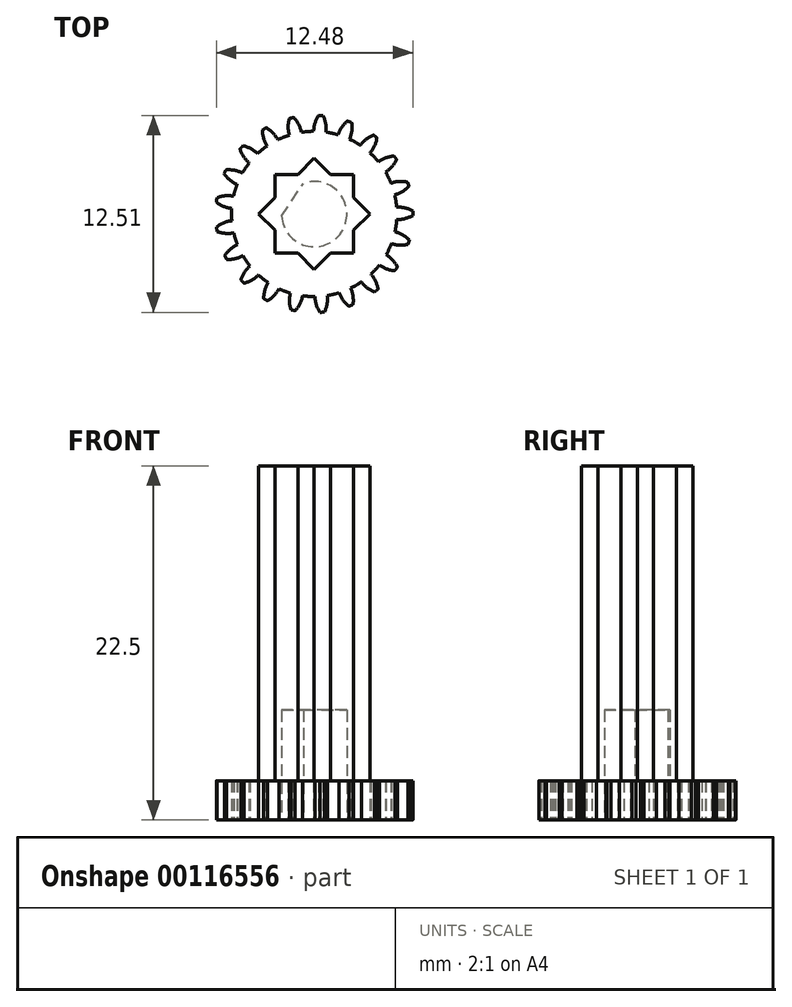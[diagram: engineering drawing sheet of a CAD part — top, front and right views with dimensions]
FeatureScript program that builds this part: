
annotation { "Feature Type Name" : "Feature", "Feature Type Description" : "" }
export const myFeature = defineFeature(function(context is Context, id is Id, definition is map)
    precondition{}
    {
        {
            var Q0;
            Q0=qCreatedBy(makeId("Top.planeOp"),FACE);
            var sketch = newSketch(context, id + "F0", { "sketchPlane" : qUnion([Q0])});
            skLineSegment(sketch, "E0", {"start": v(61.42, 3.14) * mm, "end": v(65.52, 3.14) * mm, "construction": true});
            skLineSegment(sketch, "E1", {"start": v(61.42, 3.14) * mm, "end": v(65.31, 4.4) * mm, "construction": true});
            skLineSegment(sketch, "E2", {"start": v(61.42, 3.14) * mm, "end": v(65.72, 3.82) * mm, "construction": true});
            skPoint(sketch, "E3.third.point", {"position": v(57.79, 0) * mm});
            skArc(sketch, "E4.MirrorCS", {"start": v(62.86, 3.22) * mm, "mid": v(63.38, 3.1) * mm, "end": v(63.92, 3.14) * mm});
            skArc(sketch, "E5.MirrorCS", {"start": v(62.86, 3.22) * mm, "mid": v(62.85, 3.3) * mm, "end": v(62.84, 3.36) * mm});
            skArc(sketch, "E6.MirrorCS", {"start": v(62.82, 3.5) * mm, "mid": v(62.83, 3.43) * mm, "end": v(62.84, 3.36) * mm});
            skArc(sketch, "E7.MirrorCS", {"start": v(62.82, 3.5) * mm, "mid": v(63.28, 3.78) * mm, "end": v(63.8, 3.9) * mm});
            skLineSegment(sketch, "E8", {"start": v(69.03, 4.34) * mm, "end": v(63.8, 3.9) * mm, "construction": true});
            skArc(sketch, "E9.1.0", {"start": v(63.34, 1.7) * mm, "mid": v(63.7, 2.1) * mm, "end": v(64.15, 2.39) * mm});
            skArc(sketch, "E9.1.1", {"start": v(63.34, 1.7) * mm, "mid": v(63.37, 1.64) * mm, "end": v(63.4, 1.58) * mm});
            skArc(sketch, "E9.1.2", {"start": v(63.46, 1.46) * mm, "mid": v(63.43, 1.52) * mm, "end": v(63.4, 1.58) * mm});
            skArc(sketch, "E9.1.3", {"start": v(63.46, 1.46) * mm, "mid": v(64, 1.5) * mm, "end": v(64.5, 1.68) * mm});
            skArc(sketch, "E9.2.0", {"start": v(64.37, 0.15) * mm, "mid": v(64.6, 0.63) * mm, "end": v(64.95, 1.04) * mm});
            skArc(sketch, "E9.2.1", {"start": v(64.37, 0.15) * mm, "mid": v(64.42, 0.1) * mm, "end": v(64.46, 0.05) * mm});
            skArc(sketch, "E9.2.2", {"start": v(64.56, -0.05) * mm, "mid": v(64.51, 0) * mm, "end": v(64.46, 0.05) * mm});
            skArc(sketch, "E9.2.3", {"start": v(64.56, -0.05) * mm, "mid": v(65.06, 0.14) * mm, "end": v(65.48, 0.47) * mm});
            skArc(sketch, "E9.3.0", {"start": v(65.81, -1.04) * mm, "mid": v(65.88, -0.5) * mm, "end": v(66.1, -0.02) * mm});
            skArc(sketch, "E9.3.1", {"start": v(65.81, -1.04) * mm, "mid": v(65.87, -1.07) * mm, "end": v(65.93, -1.1) * mm});
            skArc(sketch, "E9.3.2", {"start": v(66.06, -1.17) * mm, "mid": v(66, -1.14) * mm, "end": v(65.93, -1.1) * mm});
            skArc(sketch, "E9.3.3", {"start": v(66.06, -1.17) * mm, "mid": v(66.47, -0.84) * mm, "end": v(66.78, -0.4) * mm});
            skArc(sketch, "E9.4.0", {"start": v(67.54, -1.74) * mm, "mid": v(67.45, -1.22) * mm, "end": v(67.52, -0.69) * mm});
            skArc(sketch, "E9.4.1", {"start": v(67.54, -1.74) * mm, "mid": v(67.6, -1.76) * mm, "end": v(67.68, -1.78) * mm});
            skArc(sketch, "E9.4.2", {"start": v(67.81, -1.8) * mm, "mid": v(67.75, -1.8) * mm, "end": v(67.68, -1.78) * mm});
            skArc(sketch, "E9.4.3", {"start": v(67.81, -1.8) * mm, "mid": v(68.12, -1.36) * mm, "end": v(68.28, -0.85) * mm});
            skArc(sketch, "E9.5.0", {"start": v(69.4, -1.91) * mm, "mid": v(69.16, -1.43) * mm, "end": v(69.07, -0.9) * mm});
            skArc(sketch, "E9.5.1", {"start": v(69.4, -1.91) * mm, "mid": v(69.47, -1.9) * mm, "end": v(69.54, -1.9) * mm});
            skArc(sketch, "E9.5.2", {"start": v(69.68, -1.89) * mm, "mid": v(69.61, -1.9) * mm, "end": v(69.54, -1.9) * mm});
            skArc(sketch, "E9.5.3", {"start": v(69.68, -1.89) * mm, "mid": v(69.84, -1.38) * mm, "end": v(69.85, -0.84) * mm});
            skArc(sketch, "E9.6.0", {"start": v(71.23, -1.52) * mm, "mid": v(70.86, -1.14) * mm, "end": v(70.61, -0.66) * mm});
            skArc(sketch, "E9.6.1", {"start": v(71.23, -1.52) * mm, "mid": v(71.3, -1.5) * mm, "end": v(71.36, -1.47) * mm});
            skArc(sketch, "E9.6.2", {"start": v(71.49, -1.42) * mm, "mid": v(71.42, -1.45) * mm, "end": v(71.36, -1.47) * mm});
            skArc(sketch, "E9.6.3", {"start": v(71.49, -1.42) * mm, "mid": v(71.49, -0.88) * mm, "end": v(71.34, -0.37) * mm});
            skArc(sketch, "E9.7.0", {"start": v(72.86, -0.61) * mm, "mid": v(72.4, -0.35) * mm, "end": v(72.02, 0.03) * mm});
            skArc(sketch, "E9.7.1", {"start": v(72.86, -0.61) * mm, "mid": v(72.91, -0.57) * mm, "end": v(72.97, -0.53) * mm});
            skArc(sketch, "E9.7.2", {"start": v(73.08, -0.44) * mm, "mid": v(73.02, -0.48) * mm, "end": v(72.97, -0.53) * mm});
            skArc(sketch, "E9.7.3", {"start": v(73.08, -0.44) * mm, "mid": v(72.92, 0.07) * mm, "end": v(72.62, 0.52) * mm});
            skArc(sketch, "E9.8.0", {"start": v(74.15, 0.74) * mm, "mid": v(73.63, 0.85) * mm, "end": v(73.16, 1.1) * mm});
            skArc(sketch, "E9.8.1", {"start": v(74.15, 0.74) * mm, "mid": v(74.19, 0.8) * mm, "end": v(74.23, 0.85) * mm});
            skArc(sketch, "E9.8.2", {"start": v(74.3, 0.97) * mm, "mid": v(74.27, 0.9) * mm, "end": v(74.23, 0.85) * mm});
            skArc(sketch, "E9.8.3", {"start": v(74.3, 0.97) * mm, "mid": v(74, 1.41) * mm, "end": v(73.6, 1.75) * mm});
            skArc(sketch, "E9.9.0", {"start": v(74.98, 2.4) * mm, "mid": v(74.45, 2.36) * mm, "end": v(73.93, 2.46) * mm});
            skArc(sketch, "E9.9.1", {"start": v(74.98, 2.4) * mm, "mid": v(75, 2.47) * mm, "end": v(75.03, 2.54) * mm});
            skArc(sketch, "E9.9.2", {"start": v(75.06, 2.67) * mm, "mid": v(75.05, 2.6) * mm, "end": v(75.03, 2.54) * mm});
            skArc(sketch, "E9.9.3", {"start": v(75.06, 2.67) * mm, "mid": v(74.65, 3) * mm, "end": v(74.15, 3.21) * mm});
            skArc(sketch, "E9.10.0", {"start": v(75.29, 4.25) * mm, "mid": v(74.8, 4.05) * mm, "end": v(74.26, 4) * mm});
            skArc(sketch, "E9.10.1", {"start": v(75.29, 4.25) * mm, "mid": v(75.3, 4.32) * mm, "end": v(75.3, 4.39) * mm});
            skArc(sketch, "E9.10.2", {"start": v(75.29, 4.53) * mm, "mid": v(75.3, 4.46) * mm, "end": v(75.3, 4.39) * mm});
            skArc(sketch, "E9.10.3", {"start": v(75.29, 4.53) * mm, "mid": v(74.8, 4.72) * mm, "end": v(74.26, 4.77) * mm});
            skArc(sketch, "E9.11.0", {"start": v(75.04, 6.1) * mm, "mid": v(74.63, 5.76) * mm, "end": v(74.13, 5.55) * mm});
            skArc(sketch, "E9.11.1", {"start": v(75.04, 6.1) * mm, "mid": v(75.02, 6.17) * mm, "end": v(75, 6.23) * mm});
            skArc(sketch, "E9.11.2", {"start": v(74.95, 6.37) * mm, "mid": v(74.98, 6.3) * mm, "end": v(75, 6.23) * mm});
            skArc(sketch, "E9.11.3", {"start": v(74.95, 6.37) * mm, "mid": v(74.42, 6.4) * mm, "end": v(73.9, 6.3) * mm});
            skArc(sketch, "E9.12.0", {"start": v(74.25, 7.8) * mm, "mid": v(73.96, 7.35) * mm, "end": v(73.55, 7) * mm});
            skArc(sketch, "E9.12.1", {"start": v(74.25, 7.8) * mm, "mid": v(74.22, 7.85) * mm, "end": v(74.18, 7.91) * mm});
            skArc(sketch, "E9.12.2", {"start": v(74.1, 8.02) * mm, "mid": v(74.14, 7.97) * mm, "end": v(74.18, 7.91) * mm});
            skArc(sketch, "E9.12.3", {"start": v(74.1, 8.02) * mm, "mid": v(73.57, 7.9) * mm, "end": v(73.1, 7.65) * mm});
            skArc(sketch, "E9.13.0", {"start": v(73, 9.18) * mm, "mid": v(72.85, 8.67) * mm, "end": v(72.57, 8.22) * mm});
            skArc(sketch, "E9.13.1", {"start": v(73, 9.18) * mm, "mid": v(72.95, 9.23) * mm, "end": v(72.9, 9.27) * mm});
            skArc(sketch, "E9.13.2", {"start": v(72.78, 9.35) * mm, "mid": v(72.84, 9.31) * mm, "end": v(72.9, 9.27) * mm});
            skArc(sketch, "E9.13.3", {"start": v(72.78, 9.35) * mm, "mid": v(72.32, 9.09) * mm, "end": v(71.95, 8.7) * mm});
            skArc(sketch, "E9.14.0", {"start": v(71.4, 10.14) * mm, "mid": v(71.4, 9.6) * mm, "end": v(71.27, 9.09) * mm});
            skArc(sketch, "E9.14.1", {"start": v(71.4, 10.14) * mm, "mid": v(71.34, 10.17) * mm, "end": v(71.27, 10.2) * mm});
            skArc(sketch, "E9.14.2", {"start": v(71.14, 10.24) * mm, "mid": v(71.2, 10.22) * mm, "end": v(71.27, 10.2) * mm});
            skArc(sketch, "E9.14.3", {"start": v(71.14, 10.24) * mm, "mid": v(70.78, 9.85) * mm, "end": v(70.54, 9.37) * mm});
            skArc(sketch, "E9.15.0", {"start": v(69.59, 10.58) * mm, "mid": v(69.75, 10.07) * mm, "end": v(69.77, 9.54) * mm});
            skArc(sketch, "E9.15.1", {"start": v(69.59, 10.58) * mm, "mid": v(69.52, 10.59) * mm, "end": v(69.45, 10.6) * mm});
            skArc(sketch, "E9.15.2", {"start": v(69.3, 10.6) * mm, "mid": v(69.38, 10.6) * mm, "end": v(69.45, 10.6) * mm});
            skArc(sketch, "E9.15.3", {"start": v(69.3, 10.6) * mm, "mid": v(69.07, 10.12) * mm, "end": v(68.99, 9.6) * mm});
            skArc(sketch, "E9.16.0", {"start": v(67.72, 10.47) * mm, "mid": v(68.03, 10.03) * mm, "end": v(68.2, 9.53) * mm});
            skArc(sketch, "E9.16.1", {"start": v(67.72, 10.47) * mm, "mid": v(67.65, 10.46) * mm, "end": v(67.59, 10.44) * mm});
            skArc(sketch, "E9.16.2", {"start": v(67.45, 10.4) * mm, "mid": v(67.52, 10.42) * mm, "end": v(67.59, 10.44) * mm});
            skArc(sketch, "E9.16.3", {"start": v(67.45, 10.4) * mm, "mid": v(67.37, 9.88) * mm, "end": v(67.44, 9.35) * mm});
            skArc(sketch, "E9.17.0", {"start": v(65.97, 9.81) * mm, "mid": v(66.4, 9.49) * mm, "end": v(66.71, 9.05) * mm});
            skArc(sketch, "E9.17.1", {"start": v(65.97, 9.81) * mm, "mid": v(65.91, 9.78) * mm, "end": v(65.85, 9.75) * mm});
            skArc(sketch, "E9.17.2", {"start": v(65.73, 9.67) * mm, "mid": v(65.8, 9.7) * mm, "end": v(65.85, 9.75) * mm});
            skArc(sketch, "E9.17.3", {"start": v(65.73, 9.67) * mm, "mid": v(65.81, 9.14) * mm, "end": v(66.04, 8.66) * mm});
            skArc(sketch, "E9.18.0", {"start": v(64.5, 8.67) * mm, "mid": v(65, 8.48) * mm, "end": v(65.43, 8.16) * mm});
            skArc(sketch, "E9.18.1", {"start": v(64.5, 8.67) * mm, "mid": v(64.45, 8.62) * mm, "end": v(64.4, 8.57) * mm});
            skArc(sketch, "E9.18.2", {"start": v(64.3, 8.47) * mm, "mid": v(64.35, 8.52) * mm, "end": v(64.4, 8.57) * mm});
            skArc(sketch, "E9.18.3", {"start": v(64.3, 8.47) * mm, "mid": v(64.54, 7.98) * mm, "end": v(64.9, 7.59) * mm});
            skArc(sketch, "E9.19.0", {"start": v(63.42, 7.14) * mm, "mid": v(63.96, 7.11) * mm, "end": v(64.46, 6.93) * mm});
            skArc(sketch, "E9.19.1", {"start": v(63.42, 7.14) * mm, "mid": v(63.4, 7.08) * mm, "end": v(63.36, 7.02) * mm});
            skArc(sketch, "E9.19.2", {"start": v(63.3, 6.9) * mm, "mid": v(63.33, 6.96) * mm, "end": v(63.36, 7.02) * mm});
            skArc(sketch, "E9.19.3", {"start": v(63.3, 6.9) * mm, "mid": v(63.67, 6.5) * mm, "end": v(64.12, 6.22) * mm});
            skArc(sketch, "E9.20.0", {"start": v(62.85, 5.37) * mm, "mid": v(63.36, 5.5) * mm, "end": v(63.9, 5.47) * mm});
            skArc(sketch, "E9.20.1", {"start": v(62.85, 5.37) * mm, "mid": v(62.83, 5.3) * mm, "end": v(62.82, 5.23) * mm});
            skArc(sketch, "E9.20.2", {"start": v(62.8, 5.1) * mm, "mid": v(62.81, 5.16) * mm, "end": v(62.82, 5.23) * mm});
            skArc(sketch, "E9.20.3", {"start": v(62.8, 5.1) * mm, "mid": v(63.27, 4.82) * mm, "end": v(63.79, 4.7) * mm});
            skPoint(sketch, "E9.center", {"position": v(69.03, 4.34) * mm});
            skCircle(sketch, "E10", {"center": v(69.03, 4.34) * mm, "radius": 5.25 * mm});
            skSolve(sketch);
        }
        {
            var Q0;
            Q0=qSketchRegion(id+"F0",true);
            extrude(context, id + "F1", {"entities" : qUnion([Q0]), "depth" : 2.5 * mm});
        }
        {
            var Q0;
            Q0=makeQuery(id+"F1.opExtrude","CAP_FACE",FACE,{"disambiguationData":[OSD([sQuery(id+"F0.wireOp",EDGE,"E4.MirrorCS"),sQuery(id+"F0.wireOp",EDGE,"E5.MirrorCS"),sQuery(id+"F0.wireOp",EDGE,"E6.MirrorCS"),sQuery(id+"F0.wireOp",EDGE,"E7.MirrorCS"),sQuery(id+"F0.wireOp",EDGE,"3aad1c11-f46f-48f3-83f1-c81cc0587eb40.MirrorCS"),sQuery(id+"F0.wireOp",EDGE,"261d038e-785b-489d-9701-d77bc27e36f7.1.0"),sQuery(id+"F0.wireOp",EDGE,"261d038e-785b-489d-9701-d77bc27e36f7.1.1"),sQuery(id+"F0.wireOp",EDGE,"261d038e-785b-489d-9701-d77bc27e36f7.1.2"),sQuery(id+"F0.wireOp",EDGE,"261d038e-785b-489d-9701-d77bc27e36f7.1.3"),sQuery(id+"F0.wireOp",EDGE,"261d038e-785b-489d-9701-d77bc27e36f7.1.4"),sQuery(id+"F0.wireOp",EDGE,"261d038e-785b-489d-9701-d77bc27e36f7.2.0"),sQuery(id+"F0.wireOp",EDGE,"261d038e-785b-489d-9701-d77bc27e36f7.2.1"),sQuery(id+"F0.wireOp",EDGE,"261d038e-785b-489d-9701-d77bc27e36f7.2.2"),sQuery(id+"F0.wireOp",EDGE,"261d038e-785b-489d-9701-d77bc27e36f7.2.3"),sQuery(id+"F0.wireOp",EDGE,"261d038e-785b-489d-9701-d77bc27e36f7.2.4"),sQuery(id+"F0.wireOp",EDGE,"261d038e-785b-489d-9701-d77bc27e36f7.3.0"),sQuery(id+"F0.wireOp",EDGE,"261d038e-785b-489d-9701-d77bc27e36f7.3.1"),sQuery(id+"F0.wireOp",EDGE,"261d038e-785b-489d-9701-d77bc27e36f7.3.2"),sQuery(id+"F0.wireOp",EDGE,"261d038e-785b-489d-9701-d77bc27e36f7.3.3"),sQuery(id+"F0.wireOp",EDGE,"261d038e-785b-489d-9701-d77bc27e36f7.3.4"),sQuery(id+"F0.wireOp",EDGE,"261d038e-785b-489d-9701-d77bc27e36f7.4.0"),sQuery(id+"F0.wireOp",EDGE,"261d038e-785b-489d-9701-d77bc27e36f7.4.1"),sQuery(id+"F0.wireOp",EDGE,"261d038e-785b-489d-9701-d77bc27e36f7.4.2"),sQuery(id+"F0.wireOp",EDGE,"261d038e-785b-489d-9701-d77bc27e36f7.4.3"),sQuery(id+"F0.wireOp",EDGE,"261d038e-785b-489d-9701-d77bc27e36f7.4.4"),sQuery(id+"F0.wireOp",EDGE,"261d038e-785b-489d-9701-d77bc27e36f7.5.0"),sQuery(id+"F0.wireOp",EDGE,"261d038e-785b-489d-9701-d77bc27e36f7.5.1"),sQuery(id+"F0.wireOp",EDGE,"261d038e-785b-489d-9701-d77bc27e36f7.5.2"),sQuery(id+"F0.wireOp",EDGE,"261d038e-785b-489d-9701-d77bc27e36f7.5.3"),sQuery(id+"F0.wireOp",EDGE,"261d038e-785b-489d-9701-d77bc27e36f7.5.4"),sQuery(id+"F0.wireOp",EDGE,"261d038e-785b-489d-9701-d77bc27e36f7.6.0"),sQuery(id+"F0.wireOp",EDGE,"261d038e-785b-489d-9701-d77bc27e36f7.6.1"),sQuery(id+"F0.wireOp",EDGE,"261d038e-785b-489d-9701-d77bc27e36f7.6.2"),sQuery(id+"F0.wireOp",EDGE,"261d038e-785b-489d-9701-d77bc27e36f7.6.3"),sQuery(id+"F0.wireOp",EDGE,"261d038e-785b-489d-9701-d77bc27e36f7.6.4"),sQuery(id+"F0.wireOp",EDGE,"261d038e-785b-489d-9701-d77bc27e36f7.7.0"),sQuery(id+"F0.wireOp",EDGE,"261d038e-785b-489d-9701-d77bc27e36f7.7.1"),sQuery(id+"F0.wireOp",EDGE,"261d038e-785b-489d-9701-d77bc27e36f7.7.2"),sQuery(id+"F0.wireOp",EDGE,"261d038e-785b-489d-9701-d77bc27e36f7.7.3"),sQuery(id+"F0.wireOp",EDGE,"261d038e-785b-489d-9701-d77bc27e36f7.7.4"),sQuery(id+"F0.wireOp",EDGE,"261d038e-785b-489d-9701-d77bc27e36f7.8.0"),sQuery(id+"F0.wireOp",EDGE,"261d038e-785b-489d-9701-d77bc27e36f7.8.1"),sQuery(id+"F0.wireOp",EDGE,"261d038e-785b-489d-9701-d77bc27e36f7.8.2"),sQuery(id+"F0.wireOp",EDGE,"261d038e-785b-489d-9701-d77bc27e36f7.8.3"),sQuery(id+"F0.wireOp",EDGE,"261d038e-785b-489d-9701-d77bc27e36f7.8.4"),sQuery(id+"F0.wireOp",EDGE,"261d038e-785b-489d-9701-d77bc27e36f7.9.0"),sQuery(id+"F0.wireOp",EDGE,"261d038e-785b-489d-9701-d77bc27e36f7.9.1"),sQuery(id+"F0.wireOp",EDGE,"261d038e-785b-489d-9701-d77bc27e36f7.9.2"),sQuery(id+"F0.wireOp",EDGE,"261d038e-785b-489d-9701-d77bc27e36f7.9.3"),sQuery(id+"F0.wireOp",EDGE,"261d038e-785b-489d-9701-d77bc27e36f7.9.4"),sQuery(id+"F0.wireOp",EDGE,"261d038e-785b-489d-9701-d77bc27e36f7.10.0"),sQuery(id+"F0.wireOp",EDGE,"261d038e-785b-489d-9701-d77bc27e36f7.10.1"),sQuery(id+"F0.wireOp",EDGE,"261d038e-785b-489d-9701-d77bc27e36f7.10.2"),sQuery(id+"F0.wireOp",EDGE,"261d038e-785b-489d-9701-d77bc27e36f7.10.3"),sQuery(id+"F0.wireOp",EDGE,"261d038e-785b-489d-9701-d77bc27e36f7.10.4"),sQuery(id+"F0.wireOp",EDGE,"261d038e-785b-489d-9701-d77bc27e36f7.11.0"),sQuery(id+"F0.wireOp",EDGE,"261d038e-785b-489d-9701-d77bc27e36f7.11.1"),sQuery(id+"F0.wireOp",EDGE,"261d038e-785b-489d-9701-d77bc27e36f7.11.2"),sQuery(id+"F0.wireOp",EDGE,"261d038e-785b-489d-9701-d77bc27e36f7.11.3"),sQuery(id+"F0.wireOp",EDGE,"261d038e-785b-489d-9701-d77bc27e36f7.11.4"),sQuery(id+"F0.wireOp",EDGE,"261d038e-785b-489d-9701-d77bc27e36f7.12.0"),sQuery(id+"F0.wireOp",EDGE,"261d038e-785b-489d-9701-d77bc27e36f7.12.1"),sQuery(id+"F0.wireOp",EDGE,"261d038e-785b-489d-9701-d77bc27e36f7.12.2"),sQuery(id+"F0.wireOp",EDGE,"261d038e-785b-489d-9701-d77bc27e36f7.12.3"),sQuery(id+"F0.wireOp",EDGE,"261d038e-785b-489d-9701-d77bc27e36f7.12.4"),sQuery(id+"F0.wireOp",EDGE,"261d038e-785b-489d-9701-d77bc27e36f7.13.0"),sQuery(id+"F0.wireOp",EDGE,"261d038e-785b-489d-9701-d77bc27e36f7.13.1"),sQuery(id+"F0.wireOp",EDGE,"261d038e-785b-489d-9701-d77bc27e36f7.13.2"),sQuery(id+"F0.wireOp",EDGE,"261d038e-785b-489d-9701-d77bc27e36f7.13.3"),sQuery(id+"F0.wireOp",EDGE,"261d038e-785b-489d-9701-d77bc27e36f7.13.4"),sQuery(id+"F0.wireOp",EDGE,"261d038e-785b-489d-9701-d77bc27e36f7.14.0"),sQuery(id+"F0.wireOp",EDGE,"261d038e-785b-489d-9701-d77bc27e36f7.14.1"),sQuery(id+"F0.wireOp",EDGE,"261d038e-785b-489d-9701-d77bc27e36f7.14.2"),sQuery(id+"F0.wireOp",EDGE,"261d038e-785b-489d-9701-d77bc27e36f7.14.3"),sQuery(id+"F0.wireOp",EDGE,"261d038e-785b-489d-9701-d77bc27e36f7.14.4"),sQuery(id+"F0.wireOp",EDGE,"261d038e-785b-489d-9701-d77bc27e36f7.15.0"),sQuery(id+"F0.wireOp",EDGE,"261d038e-785b-489d-9701-d77bc27e36f7.15.1"),sQuery(id+"F0.wireOp",EDGE,"261d038e-785b-489d-9701-d77bc27e36f7.15.2"),sQuery(id+"F0.wireOp",EDGE,"261d038e-785b-489d-9701-d77bc27e36f7.15.3"),sQuery(id+"F0.wireOp",EDGE,"261d038e-785b-489d-9701-d77bc27e36f7.15.4"),sQuery(id+"F0.wireOp",EDGE,"261d038e-785b-489d-9701-d77bc27e36f7.16.0"),sQuery(id+"F0.wireOp",EDGE,"261d038e-785b-489d-9701-d77bc27e36f7.16.1"),sQuery(id+"F0.wireOp",EDGE,"261d038e-785b-489d-9701-d77bc27e36f7.16.2"),sQuery(id+"F0.wireOp",EDGE,"261d038e-785b-489d-9701-d77bc27e36f7.16.3"),sQuery(id+"F0.wireOp",EDGE,"261d038e-785b-489d-9701-d77bc27e36f7.16.4"),sQuery(id+"F0.wireOp",EDGE,"261d038e-785b-489d-9701-d77bc27e36f7.17.0"),sQuery(id+"F0.wireOp",EDGE,"261d038e-785b-489d-9701-d77bc27e36f7.17.1"),sQuery(id+"F0.wireOp",EDGE,"261d038e-785b-489d-9701-d77bc27e36f7.17.2"),sQuery(id+"F0.wireOp",EDGE,"261d038e-785b-489d-9701-d77bc27e36f7.17.3"),sQuery(id+"F0.wireOp",EDGE,"261d038e-785b-489d-9701-d77bc27e36f7.17.4"),sQuery(id+"F0.wireOp",EDGE,"261d038e-785b-489d-9701-d77bc27e36f7.18.0"),sQuery(id+"F0.wireOp",EDGE,"261d038e-785b-489d-9701-d77bc27e36f7.18.1"),sQuery(id+"F0.wireOp",EDGE,"261d038e-785b-489d-9701-d77bc27e36f7.18.2"),sQuery(id+"F0.wireOp",EDGE,"261d038e-785b-489d-9701-d77bc27e36f7.18.3"),sQuery(id+"F0.wireOp",EDGE,"261d038e-785b-489d-9701-d77bc27e36f7.18.4"),sQuery(id+"F0.wireOp",EDGE,"261d038e-785b-489d-9701-d77bc27e36f7.19.0"),sQuery(id+"F0.wireOp",EDGE,"261d038e-785b-489d-9701-d77bc27e36f7.19.1"),sQuery(id+"F0.wireOp",EDGE,"261d038e-785b-489d-9701-d77bc27e36f7.19.2"),sQuery(id+"F0.wireOp",EDGE,"261d038e-785b-489d-9701-d77bc27e36f7.19.3"),sQuery(id+"F0.wireOp",EDGE,"261d038e-785b-489d-9701-d77bc27e36f7.19.4"),sQuery(id+"F0.wireOp",EDGE,"f45ad2ee-8b84-45a9-bb91-348b52f7b137.4.20.0"),sQuery(id+"F0.wireOp",EDGE,"f45ad2ee-8b84-45a9-bb91-348b52f7b137.8.20.0"),sQuery(id+"F0.wireOp",EDGE,"f45ad2ee-8b84-45a9-bb91-348b52f7b137.12.20.0"),sQuery(id+"F0.wireOp",EDGE,"f45ad2ee-8b84-45a9-bb91-348b52f7b137.15.20.0"),sQuery(id+"F0.wireOp",EDGE,"f45ad2ee-8b84-45a9-bb91-348b52f7b137.16.20.0")])],"isStart":false});
            var sketch = newSketch(context, id + "F2", { "sketchPlane" : qUnion([Q0])});
            skLineSegment(sketch, "E11.bottom", {"start": v(71.53, 1.84) * mm, "end": v(66.53, 1.84) * mm});
            skLineSegment(sketch, "E11.top", {"start": v(71.53, 6.84) * mm, "end": v(66.53, 6.84) * mm});
            skLineSegment(sketch, "E11.left", {"start": v(71.53, 1.84) * mm, "end": v(71.53, 6.84) * mm});
            skLineSegment(sketch, "E11.right", {"start": v(66.53, 1.84) * mm, "end": v(66.53, 6.84) * mm});
            skPoint(sketch, "E11.middle", {"position": v(69.03, 4.34) * mm});
            skLineSegment(sketch, "E12", {"start": v(65.5, 4.34) * mm, "end": v(69.03, 7.88) * mm});
            skLineSegment(sketch, "E13", {"start": v(69.03, 7.88) * mm, "end": v(72.56, 4.34) * mm});
            skLineSegment(sketch, "E14", {"start": v(72.56, 4.34) * mm, "end": v(69.03, 0.8) * mm});
            skLineSegment(sketch, "E15", {"start": v(69.03, 0.8) * mm, "end": v(65.5, 4.34) * mm});
            skLineSegment(sketch, "E16", {"start": v(68.6, 9.57) * mm, "end": v(69.54, -1.9) * mm, "construction": true});
            skLineSegment(sketch, "E17", {"start": v(64, 5.85) * mm, "end": v(75.03, 2.54) * mm, "construction": true});
            skSolve(sketch);
        }
        {
            var Q0;
            Q0=qSketchRegion(id+"F2",true);
            extrude(context, id + "F3", {"entities" : qUnion([Q0]), "operationType" : NewBodyOperationType.ADD, "depth" : 20 * mm});
        }
        {
            var Q0;
            Q0=makeQuery(id+"F1.opExtrude","CAP_FACE",FACE,{"disambiguationData":[OSD([sQuery(id+"F0.wireOp",EDGE,"E4.MirrorCS"),sQuery(id+"F0.wireOp",EDGE,"E5.MirrorCS"),sQuery(id+"F0.wireOp",EDGE,"E6.MirrorCS"),sQuery(id+"F0.wireOp",EDGE,"E7.MirrorCS"),sQuery(id+"F0.wireOp",EDGE,"3aad1c11-f46f-48f3-83f1-c81cc0587eb40.MirrorCS"),sQuery(id+"F0.wireOp",EDGE,"261d038e-785b-489d-9701-d77bc27e36f7.1.0"),sQuery(id+"F0.wireOp",EDGE,"261d038e-785b-489d-9701-d77bc27e36f7.1.1"),sQuery(id+"F0.wireOp",EDGE,"261d038e-785b-489d-9701-d77bc27e36f7.1.2"),sQuery(id+"F0.wireOp",EDGE,"261d038e-785b-489d-9701-d77bc27e36f7.1.3"),sQuery(id+"F0.wireOp",EDGE,"261d038e-785b-489d-9701-d77bc27e36f7.1.4"),sQuery(id+"F0.wireOp",EDGE,"261d038e-785b-489d-9701-d77bc27e36f7.2.0"),sQuery(id+"F0.wireOp",EDGE,"261d038e-785b-489d-9701-d77bc27e36f7.2.1"),sQuery(id+"F0.wireOp",EDGE,"261d038e-785b-489d-9701-d77bc27e36f7.2.2"),sQuery(id+"F0.wireOp",EDGE,"261d038e-785b-489d-9701-d77bc27e36f7.2.3"),sQuery(id+"F0.wireOp",EDGE,"261d038e-785b-489d-9701-d77bc27e36f7.2.4"),sQuery(id+"F0.wireOp",EDGE,"261d038e-785b-489d-9701-d77bc27e36f7.3.0"),sQuery(id+"F0.wireOp",EDGE,"261d038e-785b-489d-9701-d77bc27e36f7.3.1"),sQuery(id+"F0.wireOp",EDGE,"261d038e-785b-489d-9701-d77bc27e36f7.3.2"),sQuery(id+"F0.wireOp",EDGE,"261d038e-785b-489d-9701-d77bc27e36f7.3.3"),sQuery(id+"F0.wireOp",EDGE,"261d038e-785b-489d-9701-d77bc27e36f7.3.4"),sQuery(id+"F0.wireOp",EDGE,"261d038e-785b-489d-9701-d77bc27e36f7.4.0"),sQuery(id+"F0.wireOp",EDGE,"261d038e-785b-489d-9701-d77bc27e36f7.4.1"),sQuery(id+"F0.wireOp",EDGE,"261d038e-785b-489d-9701-d77bc27e36f7.4.2"),sQuery(id+"F0.wireOp",EDGE,"261d038e-785b-489d-9701-d77bc27e36f7.4.3"),sQuery(id+"F0.wireOp",EDGE,"261d038e-785b-489d-9701-d77bc27e36f7.4.4"),sQuery(id+"F0.wireOp",EDGE,"261d038e-785b-489d-9701-d77bc27e36f7.5.0"),sQuery(id+"F0.wireOp",EDGE,"261d038e-785b-489d-9701-d77bc27e36f7.5.1"),sQuery(id+"F0.wireOp",EDGE,"261d038e-785b-489d-9701-d77bc27e36f7.5.2"),sQuery(id+"F0.wireOp",EDGE,"261d038e-785b-489d-9701-d77bc27e36f7.5.3"),sQuery(id+"F0.wireOp",EDGE,"261d038e-785b-489d-9701-d77bc27e36f7.5.4"),sQuery(id+"F0.wireOp",EDGE,"261d038e-785b-489d-9701-d77bc27e36f7.6.0"),sQuery(id+"F0.wireOp",EDGE,"261d038e-785b-489d-9701-d77bc27e36f7.6.1"),sQuery(id+"F0.wireOp",EDGE,"261d038e-785b-489d-9701-d77bc27e36f7.6.2"),sQuery(id+"F0.wireOp",EDGE,"261d038e-785b-489d-9701-d77bc27e36f7.6.3"),sQuery(id+"F0.wireOp",EDGE,"261d038e-785b-489d-9701-d77bc27e36f7.6.4"),sQuery(id+"F0.wireOp",EDGE,"261d038e-785b-489d-9701-d77bc27e36f7.7.0"),sQuery(id+"F0.wireOp",EDGE,"261d038e-785b-489d-9701-d77bc27e36f7.7.1"),sQuery(id+"F0.wireOp",EDGE,"261d038e-785b-489d-9701-d77bc27e36f7.7.2"),sQuery(id+"F0.wireOp",EDGE,"261d038e-785b-489d-9701-d77bc27e36f7.7.3"),sQuery(id+"F0.wireOp",EDGE,"261d038e-785b-489d-9701-d77bc27e36f7.7.4"),sQuery(id+"F0.wireOp",EDGE,"261d038e-785b-489d-9701-d77bc27e36f7.8.0"),sQuery(id+"F0.wireOp",EDGE,"261d038e-785b-489d-9701-d77bc27e36f7.8.1"),sQuery(id+"F0.wireOp",EDGE,"261d038e-785b-489d-9701-d77bc27e36f7.8.2"),sQuery(id+"F0.wireOp",EDGE,"261d038e-785b-489d-9701-d77bc27e36f7.8.3"),sQuery(id+"F0.wireOp",EDGE,"261d038e-785b-489d-9701-d77bc27e36f7.8.4"),sQuery(id+"F0.wireOp",EDGE,"261d038e-785b-489d-9701-d77bc27e36f7.9.0"),sQuery(id+"F0.wireOp",EDGE,"261d038e-785b-489d-9701-d77bc27e36f7.9.1"),sQuery(id+"F0.wireOp",EDGE,"261d038e-785b-489d-9701-d77bc27e36f7.9.2"),sQuery(id+"F0.wireOp",EDGE,"261d038e-785b-489d-9701-d77bc27e36f7.9.3"),sQuery(id+"F0.wireOp",EDGE,"261d038e-785b-489d-9701-d77bc27e36f7.9.4"),sQuery(id+"F0.wireOp",EDGE,"261d038e-785b-489d-9701-d77bc27e36f7.10.0"),sQuery(id+"F0.wireOp",EDGE,"261d038e-785b-489d-9701-d77bc27e36f7.10.1"),sQuery(id+"F0.wireOp",EDGE,"261d038e-785b-489d-9701-d77bc27e36f7.10.2"),sQuery(id+"F0.wireOp",EDGE,"261d038e-785b-489d-9701-d77bc27e36f7.10.3"),sQuery(id+"F0.wireOp",EDGE,"261d038e-785b-489d-9701-d77bc27e36f7.10.4"),sQuery(id+"F0.wireOp",EDGE,"261d038e-785b-489d-9701-d77bc27e36f7.11.0"),sQuery(id+"F0.wireOp",EDGE,"261d038e-785b-489d-9701-d77bc27e36f7.11.1"),sQuery(id+"F0.wireOp",EDGE,"261d038e-785b-489d-9701-d77bc27e36f7.11.2"),sQuery(id+"F0.wireOp",EDGE,"261d038e-785b-489d-9701-d77bc27e36f7.11.3"),sQuery(id+"F0.wireOp",EDGE,"261d038e-785b-489d-9701-d77bc27e36f7.11.4"),sQuery(id+"F0.wireOp",EDGE,"261d038e-785b-489d-9701-d77bc27e36f7.12.0"),sQuery(id+"F0.wireOp",EDGE,"261d038e-785b-489d-9701-d77bc27e36f7.12.1"),sQuery(id+"F0.wireOp",EDGE,"261d038e-785b-489d-9701-d77bc27e36f7.12.2"),sQuery(id+"F0.wireOp",EDGE,"261d038e-785b-489d-9701-d77bc27e36f7.12.3"),sQuery(id+"F0.wireOp",EDGE,"261d038e-785b-489d-9701-d77bc27e36f7.12.4"),sQuery(id+"F0.wireOp",EDGE,"261d038e-785b-489d-9701-d77bc27e36f7.13.0"),sQuery(id+"F0.wireOp",EDGE,"261d038e-785b-489d-9701-d77bc27e36f7.13.1"),sQuery(id+"F0.wireOp",EDGE,"261d038e-785b-489d-9701-d77bc27e36f7.13.2"),sQuery(id+"F0.wireOp",EDGE,"261d038e-785b-489d-9701-d77bc27e36f7.13.3"),sQuery(id+"F0.wireOp",EDGE,"261d038e-785b-489d-9701-d77bc27e36f7.13.4"),sQuery(id+"F0.wireOp",EDGE,"261d038e-785b-489d-9701-d77bc27e36f7.14.0"),sQuery(id+"F0.wireOp",EDGE,"261d038e-785b-489d-9701-d77bc27e36f7.14.1"),sQuery(id+"F0.wireOp",EDGE,"261d038e-785b-489d-9701-d77bc27e36f7.14.2"),sQuery(id+"F0.wireOp",EDGE,"261d038e-785b-489d-9701-d77bc27e36f7.14.3"),sQuery(id+"F0.wireOp",EDGE,"261d038e-785b-489d-9701-d77bc27e36f7.14.4"),sQuery(id+"F0.wireOp",EDGE,"261d038e-785b-489d-9701-d77bc27e36f7.15.0"),sQuery(id+"F0.wireOp",EDGE,"261d038e-785b-489d-9701-d77bc27e36f7.15.1"),sQuery(id+"F0.wireOp",EDGE,"261d038e-785b-489d-9701-d77bc27e36f7.15.2"),sQuery(id+"F0.wireOp",EDGE,"261d038e-785b-489d-9701-d77bc27e36f7.15.3"),sQuery(id+"F0.wireOp",EDGE,"261d038e-785b-489d-9701-d77bc27e36f7.15.4"),sQuery(id+"F0.wireOp",EDGE,"261d038e-785b-489d-9701-d77bc27e36f7.16.0"),sQuery(id+"F0.wireOp",EDGE,"261d038e-785b-489d-9701-d77bc27e36f7.16.1"),sQuery(id+"F0.wireOp",EDGE,"261d038e-785b-489d-9701-d77bc27e36f7.16.2"),sQuery(id+"F0.wireOp",EDGE,"261d038e-785b-489d-9701-d77bc27e36f7.16.3"),sQuery(id+"F0.wireOp",EDGE,"261d038e-785b-489d-9701-d77bc27e36f7.16.4"),sQuery(id+"F0.wireOp",EDGE,"261d038e-785b-489d-9701-d77bc27e36f7.17.0"),sQuery(id+"F0.wireOp",EDGE,"261d038e-785b-489d-9701-d77bc27e36f7.17.1"),sQuery(id+"F0.wireOp",EDGE,"261d038e-785b-489d-9701-d77bc27e36f7.17.2"),sQuery(id+"F0.wireOp",EDGE,"261d038e-785b-489d-9701-d77bc27e36f7.17.3"),sQuery(id+"F0.wireOp",EDGE,"261d038e-785b-489d-9701-d77bc27e36f7.17.4"),sQuery(id+"F0.wireOp",EDGE,"261d038e-785b-489d-9701-d77bc27e36f7.18.0"),sQuery(id+"F0.wireOp",EDGE,"261d038e-785b-489d-9701-d77bc27e36f7.18.1"),sQuery(id+"F0.wireOp",EDGE,"261d038e-785b-489d-9701-d77bc27e36f7.18.2"),sQuery(id+"F0.wireOp",EDGE,"261d038e-785b-489d-9701-d77bc27e36f7.18.3"),sQuery(id+"F0.wireOp",EDGE,"261d038e-785b-489d-9701-d77bc27e36f7.18.4"),sQuery(id+"F0.wireOp",EDGE,"261d038e-785b-489d-9701-d77bc27e36f7.19.0"),sQuery(id+"F0.wireOp",EDGE,"261d038e-785b-489d-9701-d77bc27e36f7.19.1"),sQuery(id+"F0.wireOp",EDGE,"261d038e-785b-489d-9701-d77bc27e36f7.19.2"),sQuery(id+"F0.wireOp",EDGE,"261d038e-785b-489d-9701-d77bc27e36f7.19.3"),sQuery(id+"F0.wireOp",EDGE,"261d038e-785b-489d-9701-d77bc27e36f7.19.4"),sQuery(id+"F0.wireOp",EDGE,"f45ad2ee-8b84-45a9-bb91-348b52f7b137.4.20.0"),sQuery(id+"F0.wireOp",EDGE,"f45ad2ee-8b84-45a9-bb91-348b52f7b137.8.20.0"),sQuery(id+"F0.wireOp",EDGE,"f45ad2ee-8b84-45a9-bb91-348b52f7b137.12.20.0"),sQuery(id+"F0.wireOp",EDGE,"f45ad2ee-8b84-45a9-bb91-348b52f7b137.15.20.0"),sQuery(id+"F0.wireOp",EDGE,"f45ad2ee-8b84-45a9-bb91-348b52f7b137.16.20.0")])],"isStart":true});
            var sketch = newSketch(context, id + "F4", { "sketchPlane" : qUnion([Q0])});
            skArc(sketch, "E18", {"start": v(68.33, -6.28) * mm, "mid": v(70.75, -3.18) * mm, "end": v(66.95, -4.2) * mm});
            skLineSegment(sketch, "E19", {"start": v(67.52, 0.69) * mm, "end": v(70.54, -9.37) * mm, "construction": true});
            skLineSegment(sketch, "E20", {"start": v(69.77, -9.54) * mm, "end": v(68.28, 0.85) * mm, "construction": true});
            skLineSegment(sketch, "E21", {"start": v(66.95, -4.2) * mm, "end": v(68.33, -6.28) * mm});
            skSolve(sketch);
        }
        {
            var Q0;
            Q0=qSketchRegion(id+"F4",true);
            extrude(context, id + "F5", {"entities" : qUnion([Q0]), "operationType" : NewBodyOperationType.REMOVE, "oppositeDirection" : true, "depth" : 7 * mm});
        }
    });
